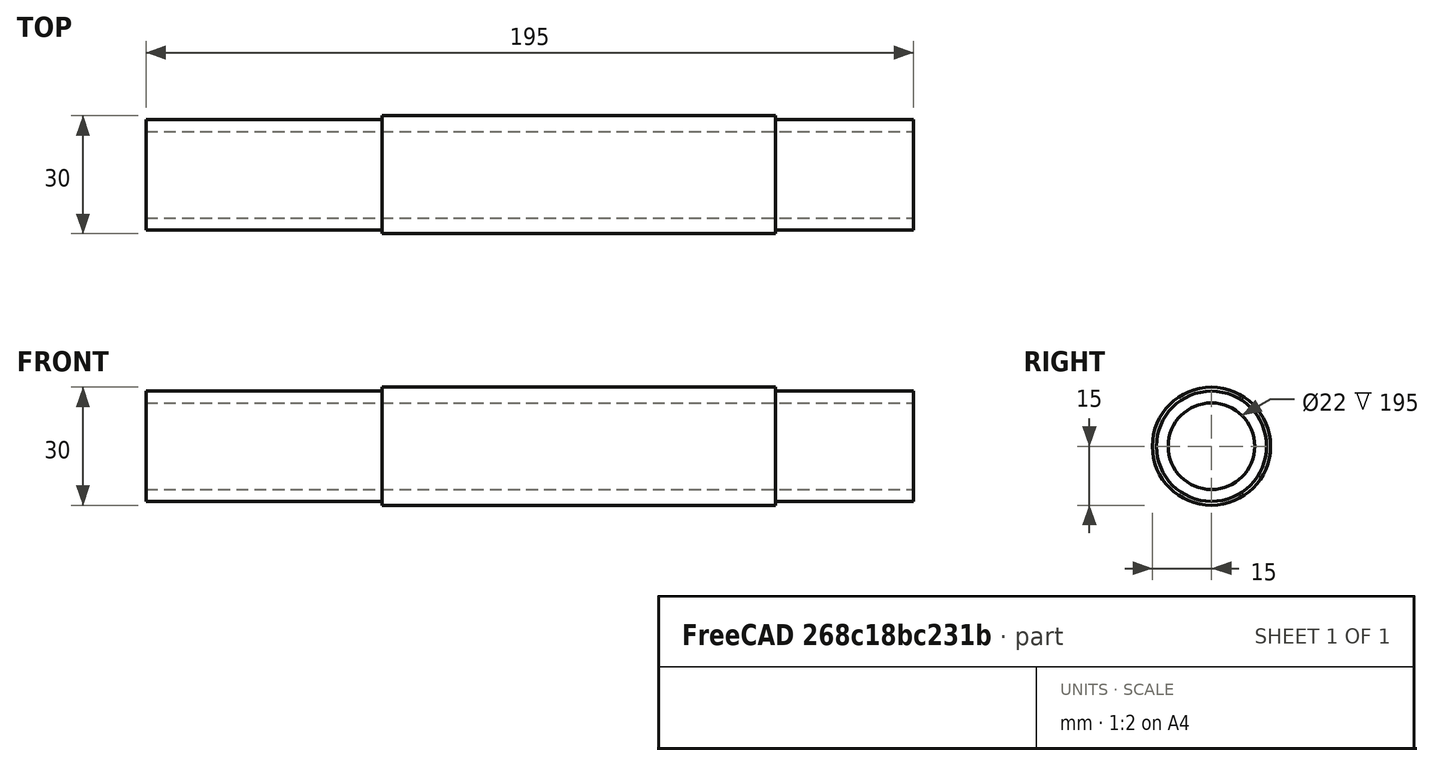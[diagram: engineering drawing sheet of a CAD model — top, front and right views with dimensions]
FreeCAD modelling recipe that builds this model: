
FCSTD DOCUMENT  (FreeCAD 0.19R24267 +99 (Git))
Label: Albero-Mandrino
License: All rights reserved
LicenseURL: http://en.wikipedia.org/wiki/All_rights_reserved
objects: Sketcher::SketchObject×1, PartDesign::Revolution×1, PartDesign::Body×1
note: 4 computed .brp shape members not serialized (recipe doc carries the construction recipe); baked Part::Feature solids carry a one-line shape summary decoded from their .brp

FEATURE [Sketcher::SketchObject] Sketch
  FullyConstrained = true
  MapMode = 5
  Support = -> [XY_Plane]
  sketch-geometry (8):
    g0: LineSegment StartX=0 StartY=-11 StartZ=0 EndX=195 EndY=-11 EndZ=0
    g1: LineSegment StartX=195 StartY=-11 StartZ=0 EndX=195 EndY=-14 EndZ=0
    g2: LineSegment StartX=195 StartY=-14 StartZ=0 EndX=160 EndY=-14 EndZ=0
    g3: LineSegment StartX=160 StartY=-14 StartZ=0 EndX=160 EndY=-15 EndZ=0
    g4: LineSegment StartX=160 StartY=-15 StartZ=0 EndX=60 EndY=-15 EndZ=0
    g5: LineSegment StartX=60 StartY=-15 StartZ=0 EndX=60 EndY=-14 EndZ=0
    g6: LineSegment StartX=60 StartY=-14 StartZ=0 EndX=0 EndY=-14 EndZ=0
    g7: LineSegment StartX=0 StartY=-14 StartZ=0 EndX=0 EndY=-11 EndZ=0
  constraints (24):
    c: PointOnObject(g0,g-2)
    c: Horizontal(g0)
    c: Coincident(g1,g0)
    c: Vertical(g1)
    c: Coincident(g2,g1)
    c: Horizontal(g2)
    c: Coincident(g3,g2)
    c: Vertical(g3)
    c: Coincident(g4,g3)
    c: Horizontal(g4)
    c: Coincident(g5,g4)
    c: Vertical(g5)
    c: PointOnObject(g6,g-2)
    c: Horizontal(g6)
    c: Coincident(g7,g0)
    c: DistanceY(g0,g-1) = 11
    c: DistanceY(g7,g7) = 3
    c: Coincident(g6,g7)
    c: Coincident(g5,g6)
    c: Equal(g1,g7)
    c: DistanceY(g5,g5) = 1
    c: DistanceX(g2,g2) = 35
    c: DistanceX(g6,g6) = 60
    c: DistanceX(g4,g4) = 100
FEATURE [PartDesign::Revolution] Revolution
  Angle = 360
  Axis = (1,0,0)
  Base = (0,0,0)
  Profile = -> Sketch
  ReferenceAxis = -> X_Axis
  Reversed = true
FEATURE [PartDesign::Body] Body
  Group = -> [Sketch,Revolution]
  Origin = -> Origin
  Tip = -> Revolution
